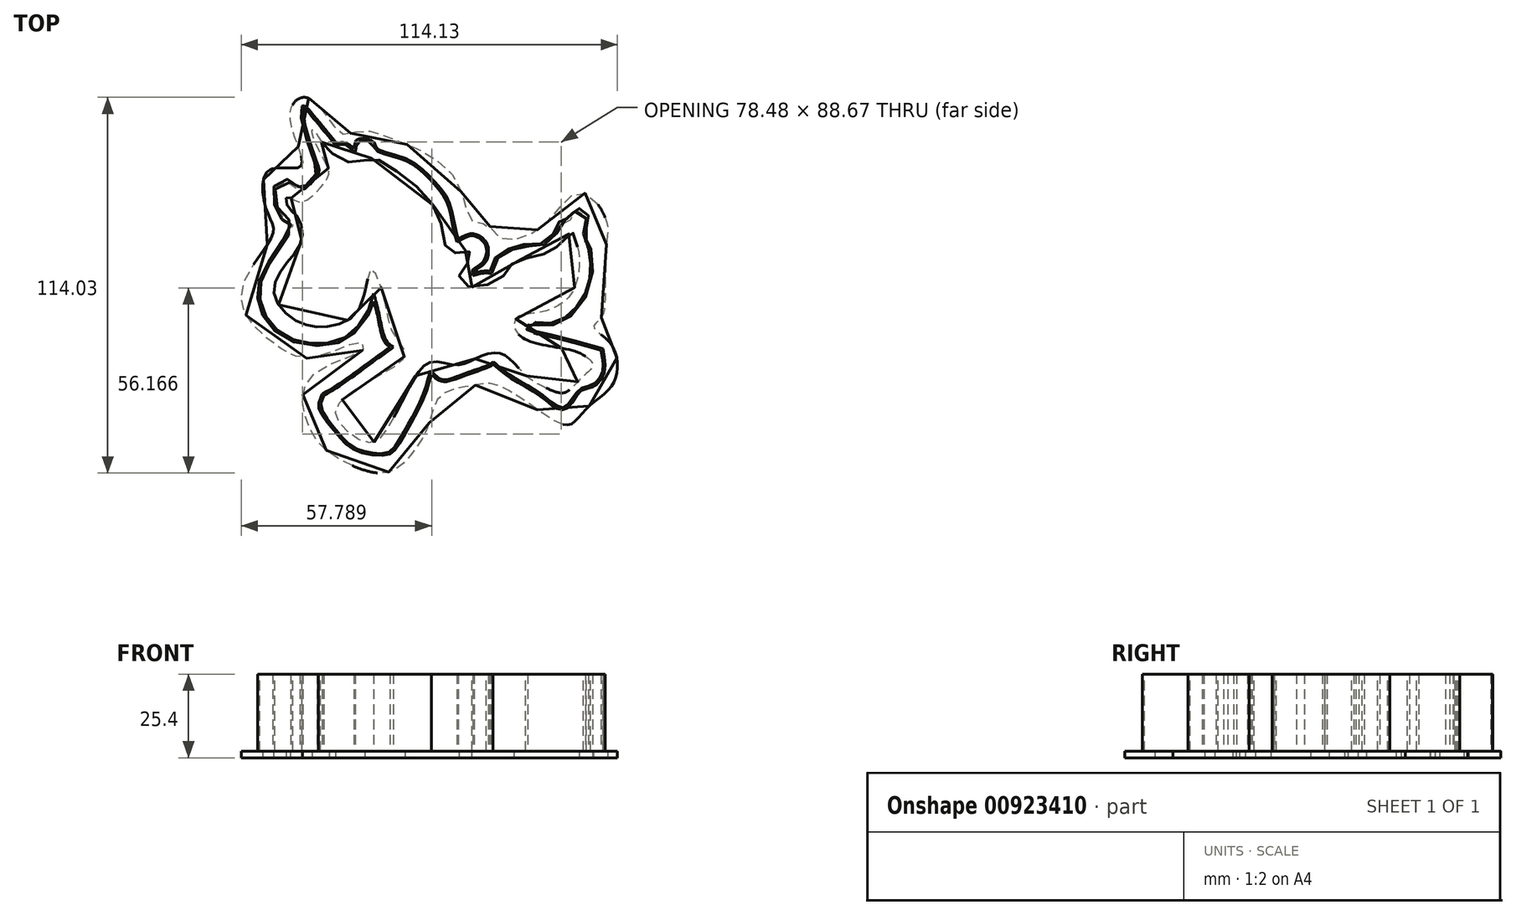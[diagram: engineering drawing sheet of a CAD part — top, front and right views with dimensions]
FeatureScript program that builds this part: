
annotation { "Feature Type Name" : "Feature", "Feature Type Description" : "" }
export const myFeature = defineFeature(function(context is Context, id is Id, definition is map)
    precondition{}
    {
        {
            var Q0;
            Q0=qCreatedBy(makeId("Top.planeOp"),FACE);
            var sketch = newSketch(context, id + "F0", { "sketchPlane" : qUnion([Q0])});
            skFitSpline(sketch, "E0", {"points": [v(21.45, 151.77) * mm, v(20.97, 149.6) * mm, v(23.25, 140.6) * mm, v(25.9, 132.91) * mm, v(25.77, 131.11) * mm, v(22.65, 127.63) * mm, v(21.09, 126.67) * mm, v(20, 127.51) * mm, v(17.25, 129.43) * mm, v(13.16, 127.63) * mm, v(13.28, 121.14) * mm, v(15.67, 117.2) * mm, v(17.88, 116.23) * mm, v(17.25, 113.46) * mm, v(10.76, 103.49) * mm, v(8.13, 96.9) * mm, v(8.55, 90.95) * mm, v(11.5, 85.34) * mm, v(19.12, 80.05) * mm, v(29.27, 79.15) * mm, v(36.05, 81.68) * mm, v(41.76, 88.46) * mm, v(43.26, 92.42) * mm], "startDerivative": vector(-73.98, -57.4) * mm, "endDerivative": vector(25.14, 90.96) * mm});
            skFitSpline(sketch, "E1", {"points": [v(43.26, 92.42) * mm, v(44.37, 87.92) * mm, v(45.49, 82.77) * mm, v(46.8, 79.74) * mm, v(48.11, 78.53) * mm], "startDerivative": vector(4.1, -15.37) * mm, "endDerivative": vector(7.81, -5.83) * mm});
            skFitSpline(sketch, "E2", {"points": [v(48.11, 78.53) * mm, v(43.26, 75) * mm, v(32.86, 67.52) * mm, v(27.6, 64.3) * mm], "startDerivative": vector(-14.66, -10.62) * mm, "endDerivative": vector(-15.96, -9.2) * mm});
            skFitSpline(sketch, "E3", {"points": [v(27.6, 64.3) * mm, v(26.73, 62.15) * mm, v(26.73, 59.6) * mm, v(31.9, 52.3) * mm, v(37.77, 47.12) * mm, v(47.36, 45.84) * mm, v(50.85, 48.99) * mm, v(58.07, 62.32) * mm, v(60.36, 68.77) * mm, v(60.78, 70.3) * mm], "startDerivative": vector(-14.1, -30.86) * mm, "endDerivative": vector(6.35, 23.1) * mm});
            skFitSpline(sketch, "E4", {"points": [v(60.78, 70.3) * mm, v(64, 68.1) * mm, v(70.2, 69.62) * mm, v(78.28, 72.6) * mm, v(79.47, 73.36) * mm], "startDerivative": vector(12.88, -12.86) * mm, "endDerivative": vector(6.17, 5.06) * mm});
            skFitSpline(sketch, "E5", {"points": [v(79.47, 73.36) * mm, v(85.07, 68.94) * mm, v(92.88, 64.3) * mm, v(98.23, 60.28) * mm, v(101.67, 59.8) * mm, v(106.05, 65.19) * mm, v(109.41, 66.36) * mm, v(113.08, 70.3) * mm, v(112.78, 78.06) * mm], "startDerivative": vector(38.3, -33.54) * mm, "endDerivative": vector(-11.46, 58.7) * mm});
            skFitSpline(sketch, "E6", {"points": [v(112.78, 78.06) * mm, v(97.77, 82.11) * mm, v(91.22, 83.62) * mm, v(90.02, 84.46) * mm, v(90.44, 85.54) * mm, v(92.6, 85.36) * mm, v(96.39, 85.12) * mm, v(102.87, 87.88) * mm, v(109.14, 98.17) * mm, v(108.92, 108.8) * mm, v(107.96, 110.6) * mm, v(107.46, 112.89) * mm, v(108.03, 115.96) * mm, v(108.17, 118.89) * mm, v(105.82, 120.6) * mm, v(103.82, 120.17) * mm, v(103.46, 118.74) * mm, v(102.46, 117.67) * mm, v(100.82, 117.6) * mm, v(99.6, 116.81) * mm, v(98.25, 113.89) * mm, v(94.68, 110.17) * mm, v(88.9, 109.74) * mm, v(83.97, 108.24) * mm, v(80.18, 105.75) * mm, v(78.54, 101.6) * mm], "startDerivative": vector(-200.41, 57.34) * mm, "endDerivative": vector(-26.14, -105.67) * mm});
            skFitSpline(sketch, "E7", {"points": [v(78.54, 101.6) * mm, v(76.4, 101.6) * mm, v(73.75, 101.03) * mm], "startDerivative": vector(-4.44, 0.25) * mm, "endDerivative": vector(-5.11, -1.37) * mm});
            skFitSpline(sketch, "E8", {"points": [v(73.75, 101.03) * mm, v(73.75, 101.6) * mm, v(75.84, 103.06) * mm, v(77.8, 105.74) * mm, v(77.41, 110.33) * mm, v(73.75, 112.92) * mm, v(71.21, 112.53) * mm, v(68.83, 111.34) * mm], "startDerivative": vector(-2.7, 8.67) * mm, "endDerivative": vector(-16.97, -9.18) * mm});
            skFitSpline(sketch, "E9", {"points": [v(68.83, 111.34) * mm, v(67.8, 115.61) * mm, v(66, 122.88) * mm, v(61.24, 129.32) * mm, v(53.38, 135.6) * mm, v(44.28, 138.7) * mm, v(43.68, 140.03) * mm, v(42.54, 141.35) * mm, v(38.76, 141.83) * mm, v(37.68, 140.93) * mm, v(37.2, 138.82) * mm], "startDerivative": vector(-10.5, 38.27) * mm, "endDerivative": vector(-4.96, -33.09) * mm});
            skFitSpline(sketch, "E10", {"points": [v(21.45, 151.77) * mm, v(23.5, 150.66) * mm, v(27.77, 145.57) * mm, v(31.05, 141.58) * mm, v(32.09, 140.54) * mm, v(33.48, 140.72) * mm, v(35.2, 140.34) * mm, v(37.2, 138.82) * mm], "startDerivative": vector(14.5, 8.54) * mm, "endDerivative": vector(14.62, -12.8) * mm});
            skSolve(sketch);
        }
        {
            var Q0;
            Q0=makeQuery(id+"F0.imprint","IMPRINT",FACE,{"disambiguationData":[TD([[makeQuery(id+"F0.imprint","IMPRINT",EDGE,{"derivedFrom":sQuery(id+"F0.wireOp",EDGE,"E0")}),1.0]])]});
            extrude(context, id + "F1", {"entities" : qUnion([Q0]), "depth" : 25.4 * mm, "offsetDistance" : 25.4 * mm});
        }
        {
            var Q0;
            Q0=makeQuery(id+"F1.opExtrude","CAP_FACE",FACE,{"disambiguationData":[OSD([sQuery(id+"F0.wireOp",EDGE,"E0"),sQuery(id+"F0.wireOp",EDGE,"E1"),sQuery(id+"F0.wireOp",EDGE,"E2"),sQuery(id+"F0.wireOp",EDGE,"E3"),sQuery(id+"F0.wireOp",EDGE,"E4"),sQuery(id+"F0.wireOp",EDGE,"E5"),sQuery(id+"F0.wireOp",EDGE,"E6"),sQuery(id+"F0.wireOp",EDGE,"E7"),sQuery(id+"F0.wireOp",EDGE,"E8"),sQuery(id+"F0.wireOp",EDGE,"E9"),sQuery(id+"F0.wireOp",EDGE,"E10")])],"isStart":false});
            shell(context, id + "F2", {"entities" : qUnion([Q0]), "thickness" : 0.64 * mm});
        }
        {
            var Q0;
            Q0=makeQuery(id+"F2.opShell","OFFSET_FACE",FACE,{"disambiguationData":[OSD([sQuery(id+"F0.wireOp",EDGE,"E0"),sQuery(id+"F0.wireOp",EDGE,"E1"),sQuery(id+"F0.wireOp",EDGE,"E2"),sQuery(id+"F0.wireOp",EDGE,"E3"),sQuery(id+"F0.wireOp",EDGE,"E4"),sQuery(id+"F0.wireOp",EDGE,"E5"),sQuery(id+"F0.wireOp",EDGE,"E6"),sQuery(id+"F0.wireOp",EDGE,"E7"),sQuery(id+"F0.wireOp",EDGE,"E8"),sQuery(id+"F0.wireOp",EDGE,"E9"),sQuery(id+"F0.wireOp",EDGE,"E10")])]});
            extrude(context, id + "F3", {"entities" : qUnion([Q0]), "operationType" : NewBodyOperationType.REMOVE, "oppositeDirection" : true, "depth" : 25.4 * mm, "offsetDistance" : 25.4 * mm});
        }
        {
            var Q0;
            Q0=qCreatedBy(makeId("Top.planeOp"),FACE);
            var sketch = newSketch(context, id + "F4", { "sketchPlane" : qUnion([Q0])});
            skFitSpline(sketch, "E11", {"points": [v(27.37, 140.8) * mm, v(31.52, 136.66) * mm, v(38.01, 134.45) * mm, v(42.58, 135.83) * mm, v(49.9, 132.1) * mm, v(59.99, 123.4) * mm, v(64.14, 113.72) * mm, v(66.48, 107.09) * mm, v(71.46, 107.92) * mm, v(72.84, 105.57) * mm, v(69.39, 101.42) * mm, v(70.77, 97.41) * mm, v(77.96, 97.55) * mm, v(83.62, 101.28) * mm, v(86.1, 104.6) * mm, v(93.02, 106.12) * mm, v(97.72, 108.33) * mm, v(101.17, 110.96) * mm, v(103.1, 113.58) * mm, v(104.21, 111.93) * mm, v(105.6, 104.88) * mm, v(102.14, 93.4) * mm, v(92.05, 88.85) * mm, v(87.08, 87.88) * mm, v(85.83, 84.98) * mm, v(88.87, 81.1) * mm, v(97.86, 78.62) * mm, v(106.7, 76.27) * mm, v(109.6, 72.95) * mm, v(106.43, 69.36) * mm, v(101.31, 64.8) * mm, v(97.44, 65.35) * mm, v(90.95, 68.67) * mm, v(85, 74.47) * mm, v(80.86, 76.82) * mm, v(74.22, 75.16) * mm, v(68.56, 73.1) * mm, v(60.4, 73.92) * mm, v(54.05, 66.32) * mm, v(48.45, 55.67) * mm, v(42.78, 49.59) * mm, v(35.18, 53.04) * mm, v(31.73, 59.4) * mm, v(37.8, 65.75) * mm, v(47.2, 71.28) * mm, v(52.73, 76.4) * mm, v(49.14, 82.9) * mm, v(46.51, 92.98) * mm, v(42.5, 102.24) * mm, v(38.91, 90.35) * mm, v(29.24, 84.83) * mm, v(20.4, 86.2) * mm, v(13.07, 94.22) * mm, v(15.97, 102.93) * mm, v(21.22, 110.53) * mm, v(20.31, 117.9) * mm, v(17.13, 121.21) * mm, v(17, 124.11) * mm, v(20.31, 122.73) * mm, v(25.01, 124.8) * mm, v(29.57, 130.75) * mm, v(28.63, 134.5) * mm, v(24.53, 143.49) * mm, v(24.82, 144.66) * mm, v(27.37, 140.8) * mm]});
            skFitSpline(sketch, "E12", {"points": [v(23.5, 154.09) * mm, v(30.93, 145.95) * mm, v(34.42, 143.16) * mm, v(40, 144.32) * mm, v(47.66, 142.23) * mm, v(56.96, 138.51) * mm, v(67.65, 130.15) * mm, v(71.37, 120.38) * mm, v(73.93, 116.43) * mm, v(78.11, 115.5) * mm, v(80.67, 112.25) * mm, v(86.71, 111.32) * mm, v(96.24, 116.9) * mm, v(102.98, 124.34) * mm, v(108.33, 124.8) * mm, v(113.9, 116.43) * mm, v(113.9, 110.62) * mm, v(113.44, 94.82) * mm, v(112.05, 87.15) * mm, v(109.96, 84.82) * mm, v(114.84, 79.94) * mm, v(117.16, 72.27) * mm, v(114.85, 66) * mm, v(107.52, 59.64) * mm, v(102.44, 54.95) * mm, v(92.38, 59.93) * mm, v(79.57, 67.36) * mm, v(74, 66.97) * mm, v(63.93, 64.14) * mm, v(59.98, 55.3) * mm, v(54.87, 46.24) * mm, v(47.9, 40.66) * mm, v(38.6, 41.82) * mm, v(28.6, 47.4) * mm, v(24.19, 53.21) * mm, v(21.63, 63.2) * mm, v(27.44, 72.04) * mm, v(40.46, 78.31) * mm, v(39.3, 79.94) * mm, v(24.89, 75.3) * mm, v(13.35, 79.33) * mm, v(3.97, 89.3) * mm, v(4.95, 100.64) * mm, v(12.77, 113.54) * mm, v(10.62, 120.38) * mm, v(11.6, 132.3) * mm, v(21.03, 133.38) * mm, v(18.68, 144.13) * mm, v(18.97, 152.64) * mm, v(23.5, 154.09) * mm]});
            skSolve(sketch);
        }
        {
            var Q0;
            Q0 = qSketchRegion(id + "F4", true);
            extrude(context, id + "F5", {"entities" : qUnion([Q0]), "operationType" : NewBodyOperationType.ADD, "depth" : 2.03 * mm, "offsetDistance" : 25.4 * mm});
        }
    });
